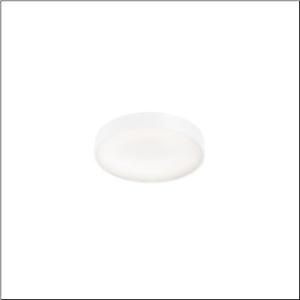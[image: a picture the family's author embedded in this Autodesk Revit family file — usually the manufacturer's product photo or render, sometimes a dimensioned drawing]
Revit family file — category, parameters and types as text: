
# Revit family: round_21_s_51mr34nd0421w
name_source: partatom
category: Lighting Fixtures
units: mm (PartAtom-declared; Revit-internal decimal feet)

## family parameters
Cut with Voids When Loaded = No
Host = Face
Light Source = No
Part Type = Normal
Room Calculation Point = No
Round Connector Dimension = Use Diameter
Shared = No

## types (1)
- Round 21 S (1 x LED, 3810 lm, 28.3 W, 4000K)
    Apparent Load = 28 VA
    CIE Flux Codes = 66 90 98 71 100
    Color Rendering = 80
    Color Temperature = 4000K
    Default Elevation = 1800 mm
    Description = Round 21 S, wall and ceiling luminaire, primary optical cover: micro prismatic cover, of PMMA, transparent, CAT 2 (L<= 3000cd/m²), light emission: direct/indirect distribution, primary light characteristic: symmetric, installation type: surface-mounted, suspended mounting, LED, rated luminous flux: 3.800lm, luminous efficacy: 135lm/W, light colour: 840, colour temperature: 4000K, control gear: DALI 2, with terminal, 5-pole, mains connection: 230V, AC, 50/60Hz, rated input power: 28.3W, housing, of aluminium, coated, white, diameter: 400mm, height: 62mm, protection rating (complete): IP40, insulation class (complete): insulation class I (protective earthing), certification: CE, impact resistance: IK04, permissible operating ambient temperature: -10..+35°C, packaging unit: 1 piece
    Height = 87 mm
    Lamp = 1 x LED
    Lamp Light Flux = 3810 lm
    Lamp Power = 28.3 W
    Lamp count = 1
    Length = 400 mm
    Luminous efficacy = 135 lm/W
    Manufacturer = Siteco
    ModVariant = No
    Model = 51MR34ND0421W
    Mounting Place = Wall
    Mounting Type = Surface mounted
    Number of Poles = 1
    OnlyDefault = Yes
    Power Factor = 1
    Product Name = Round 21 S
    Product group = wall and ceiling luminaire
    ProductGroupID = 2001
    Protection Class = Protection class I
    Protection Degree = IP 40
    RLX_Detail_Level = 1
    RLX_Emergency_Light_Flux = 0 lm
    RLX_Emergency_Type = 0
    RLX_Emergency_Type_DB = No
    RlxData = <blob elided: 12857 chars, md5=7e018162>
    Socket = socket
    Standby Power = 0 W
    System Light Flux = 3810 lm
    System Power = 28 W
    Type Comments = Product without accessories
    Type Image = l_1258334.jpg
    URL = http://relux.com
    VarID = ---
    Voltage = 0 V
    Weight = 0.00 kg
    Width = 0 mm  [stored 0 ft]

note: [stored X ft] marks values corroborated as IEEE doubles in the binary element streams (Revit-internal decimal feet)

## geometry (parser evidence)
native form markers: Sweep x11
no freeform markers — native parametric forms only
